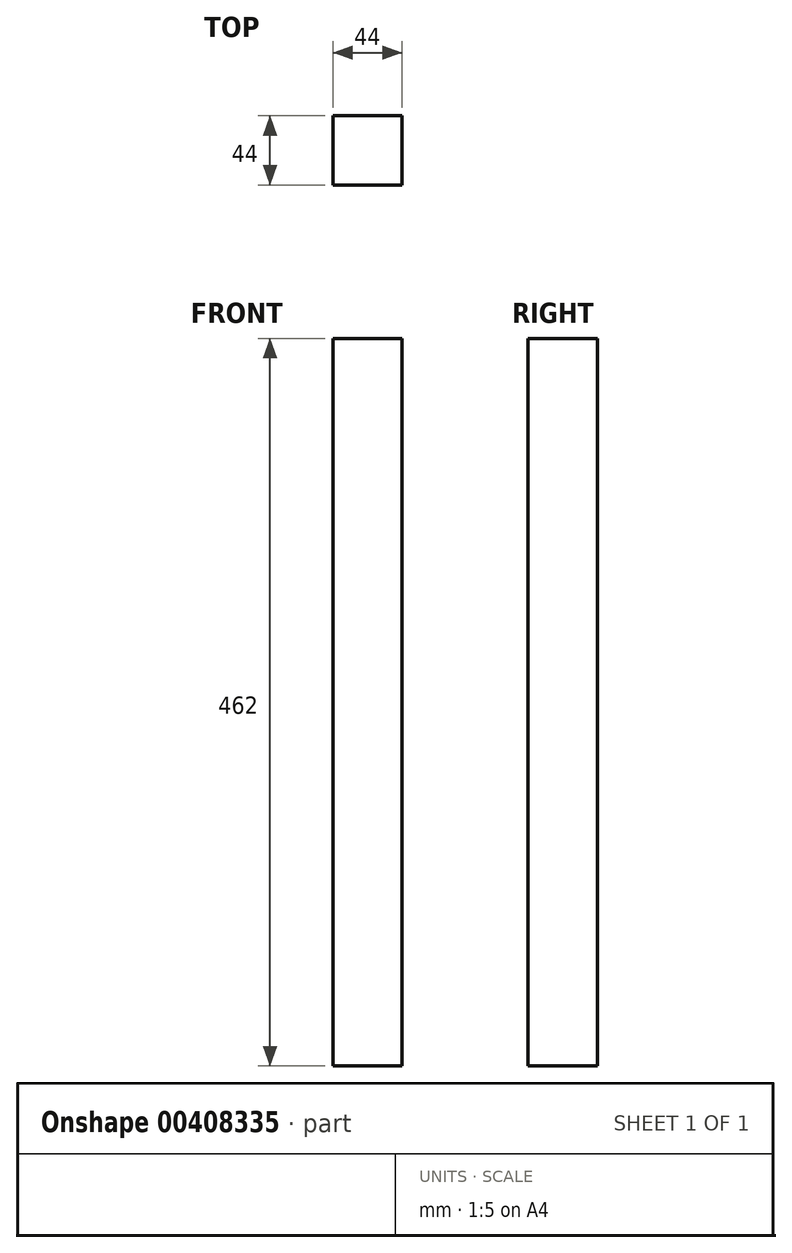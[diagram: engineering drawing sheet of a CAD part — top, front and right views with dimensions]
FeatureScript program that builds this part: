
annotation { "Feature Type Name" : "Feature", "Feature Type Description" : "" }
export const myFeature = defineFeature(function(context is Context, id is Id, definition is map)
    precondition{}
    {
        {
            var Q0;
            Q0=qCreatedBy(makeId("Top.planeOp"),FACE);
            var sketch = newSketch(context, id + "F0", { "sketchPlane" : qUnion([Q0])});
            skLineSegment(sketch, "E0.bottom", {"start": v(22, 22) * mm, "end": v(-22, 22) * mm});
            skLineSegment(sketch, "E0.top", {"start": v(22, -22) * mm, "end": v(-22, -22) * mm});
            skLineSegment(sketch, "E0.left", {"start": v(22, 22) * mm, "end": v(22, -22) * mm});
            skLineSegment(sketch, "E0.right", {"start": v(-22, 22) * mm, "end": v(-22, -22) * mm});
            skPoint(sketch, "E0.middle", {"position": v(0, 0) * mm});
            skSolve(sketch);
        }
        {
            var Q0;
            Q0=makeQuery(id+"F0.imprint","IMPRINT",FACE,{"disambiguationData":[TD([[makeQuery(id+"F0.imprint","IMPRINT",EDGE,{"derivedFrom":sQuery(id+"F0.wireOp",EDGE,"E0.bottom")}),1.0]])]});
            extrude(context, id + "F1", {"entities" : qUnion([Q0]), "depth" : (550 - 44 * 2) * mm});
        }
    });
